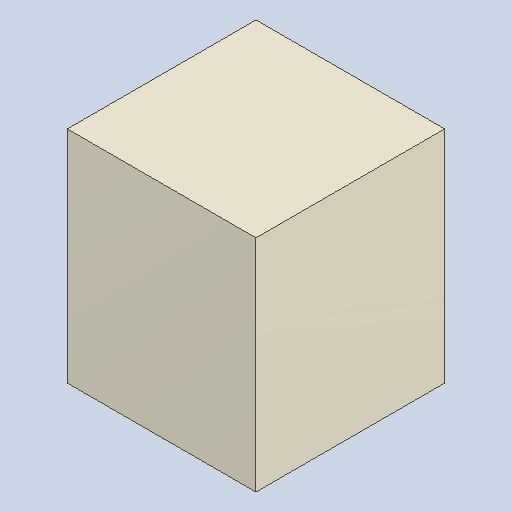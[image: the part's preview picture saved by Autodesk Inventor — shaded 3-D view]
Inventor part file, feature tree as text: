
AUTODESK INVENTOR PART (.ipt)
format: ipt  version: 2023.4 (Build 274418000, 418)  size: 82,944 bytes
history: native  units: mm
features: extrude x1
ambient origin geometry x8: Origin, YZ Plane, XZ Plane, XY Plane, X Axis, Y Axis, Z Axis, Center Point
bodies: Solid1 (feature_tree)
feature tree (1):
  extrude  "Extruded_16"  [1 undecoded]
note: 1 required parameter value undecoded (feature->parameter linkage not recoverable at this tier; creation-order binding heuristic only, values carry confidence <= 0.55)
